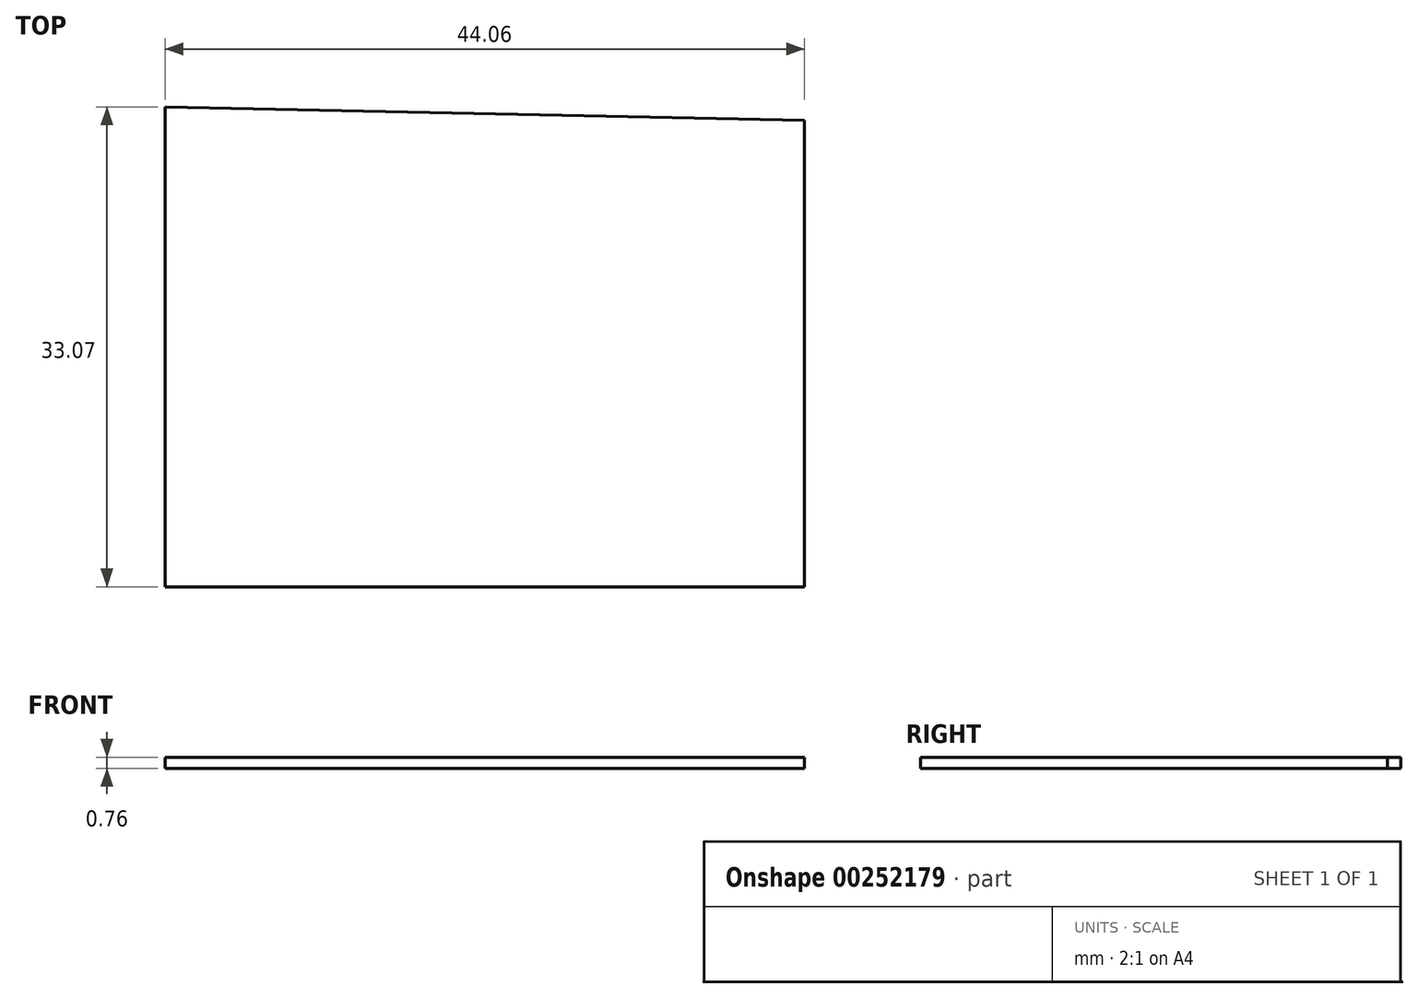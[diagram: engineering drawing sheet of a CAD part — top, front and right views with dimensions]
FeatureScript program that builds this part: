
annotation { "Feature Type Name" : "Feature", "Feature Type Description" : "" }
export const myFeature = defineFeature(function(context is Context, id is Id, definition is map)
    precondition{}
    {
        {
            var Q0;
            Q0=qCreatedBy(makeId("Top.planeOp"),FACE);
            var sketch = newSketch(context, id + "F0", { "sketchPlane" : qUnion([Q0])});
            skLineSegment(sketch, "E0", {"start": v(-44.06, 33.07) * mm, "end": v(-44.06, 0) * mm});
            skLineSegment(sketch, "E1", {"start": v(-44.06, 0) * mm, "end": v(0, 0) * mm});
            skLineSegment(sketch, "E2", {"start": v(0, 0) * mm, "end": v(0, 32.15) * mm});
            skLineSegment(sketch, "E3", {"start": v(0, 32.15) * mm, "end": v(-44.06, 33.07) * mm});
            skSolve(sketch);
        }
        {
            var Q0;
            Q0=makeQuery(id+"F0.imprint","IMPRINT",FACE,{"disambiguationData":[TD([[makeQuery(id+"F0.imprint","IMPRINT",EDGE,{"derivedFrom":sQuery(id+"F0.wireOp",EDGE,"E0")}),1.0]])]});
            extrude(context, id + "F1", {"entities" : qUnion([Q0]), "depth" : 0.76 * mm});
        }
    });
